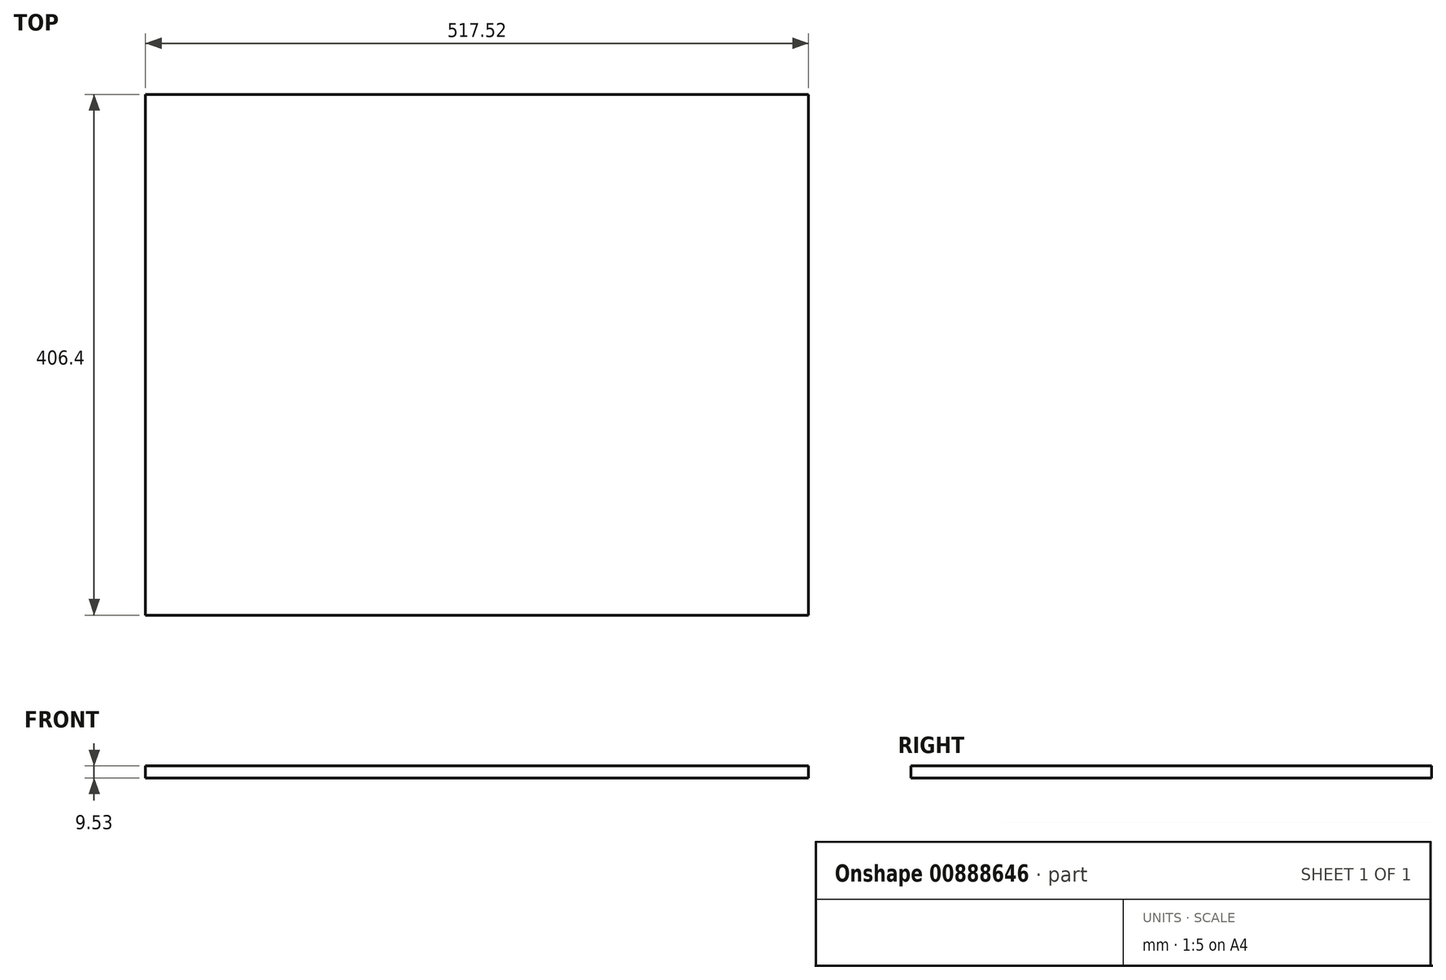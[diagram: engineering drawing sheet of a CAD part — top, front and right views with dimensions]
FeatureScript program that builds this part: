
annotation { "Feature Type Name" : "Feature", "Feature Type Description" : "" }
export const myFeature = defineFeature(function(context is Context, id is Id, definition is map)
    precondition{}
    {
        {
            var Q0;
            Q0=qCreatedBy(makeId("Top.planeOp"),FACE);
            var sketch = newSketch(context, id + "F0", { "sketchPlane" : qUnion([Q0])});
            skLineSegment(sketch, "E0.bottom", {"start": v(-258.76, 203.2) * mm, "end": v(258.76, 203.2) * mm});
            skLineSegment(sketch, "E0.top", {"start": v(-258.76, -203.2) * mm, "end": v(258.76, -203.2) * mm});
            skLineSegment(sketch, "E0.left", {"start": v(-258.76, 203.2) * mm, "end": v(-258.76, -203.2) * mm});
            skLineSegment(sketch, "E0.right", {"start": v(258.76, 203.2) * mm, "end": v(258.76, -203.2) * mm});
            skLineSegment(sketch, "E1", {"start": v(-258.76, 203.2) * mm, "end": v(258.76, -203.2) * mm, "construction": true});
            skSolve(sketch);
        }
        {
            var Q0;
            Q0 = qSketchRegion(id + "F0", true);
            extrude(context, id + "F1", {"entities" : qUnion([Q0]), "depth" : 9.52 * mm, "offsetDistance" : 25.4 * mm});
        }
    });
